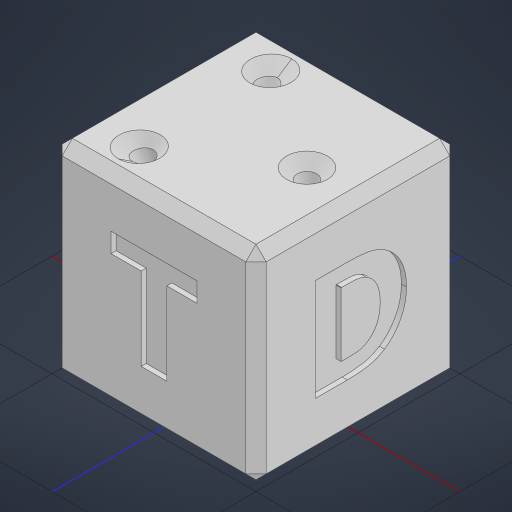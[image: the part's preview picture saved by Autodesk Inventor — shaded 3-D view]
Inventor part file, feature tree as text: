
AUTODESK INVENTOR PART (.ipt)
format: ipt  version: 2023.2 (Build 272271030, 271C)  size: 341,504 bytes
history: native  units: mm
features: sketch x7, other x6, revolve x3, extrude x1, plane x1, chamfer x1
ambient origin geometry x8: Origin, YZ Plane, XZ Plane, XY Plane, X Axis, Y Axis, Z Axis, Center Point
bodies: Volumenkörper1 (feature_tree)
feature tree (19):
  extrude  "Extrusion1"  Depth=40.0mm
  revolve  "Umdrehung1"
  plane  "Arbeitsebene1"
  sketch  "Skizze3"  dims[d4=26.0mm]
  revolve  "Umdrehung2"
  revolve  "Umdrehung3"
  chamfer  "Fase1"  [1 undecoded]
  sketch  "Skizze4"  dims[d5=2.0mm]
  sketch  "Skizze5"  dims[d6=4.0mm]
  sketch  "Skizze6"  dims[d7=10.0mm]
  sketch  "Skizze7"  dims[d8=180.0deg d9=-10.0mm d10=2.0mm d12=12.041953mm d13=4.0mm d14=26.0mm d15=5.0mm d16=90.0deg d17=90.0deg d18=2.0mm d19=2.0mm d20=45.0deg d23=1.0mm d24=0.0mm d25=1.0mm d26=0.0mm d27=1.0mm d28=0.0mm d29=1.0mm d30=0.0mm]
  other  "Prägen1"
  other  "Prägen2"
  other  "Prägen3"
  other  "Prägen4"
  sketch  "Skizze1"  dims[d0=40.0mm d2=40.0mm]
  sketch  "Skizze2"  dims[d3=0.0mm]
  other  "Schnittkanten projizieren1"
  other  "Schnittkanten projizieren2"
note: 1 required parameter value undecoded (feature->parameter linkage not recoverable at this tier; creation-order binding heuristic only, values carry confidence <= 0.55)
